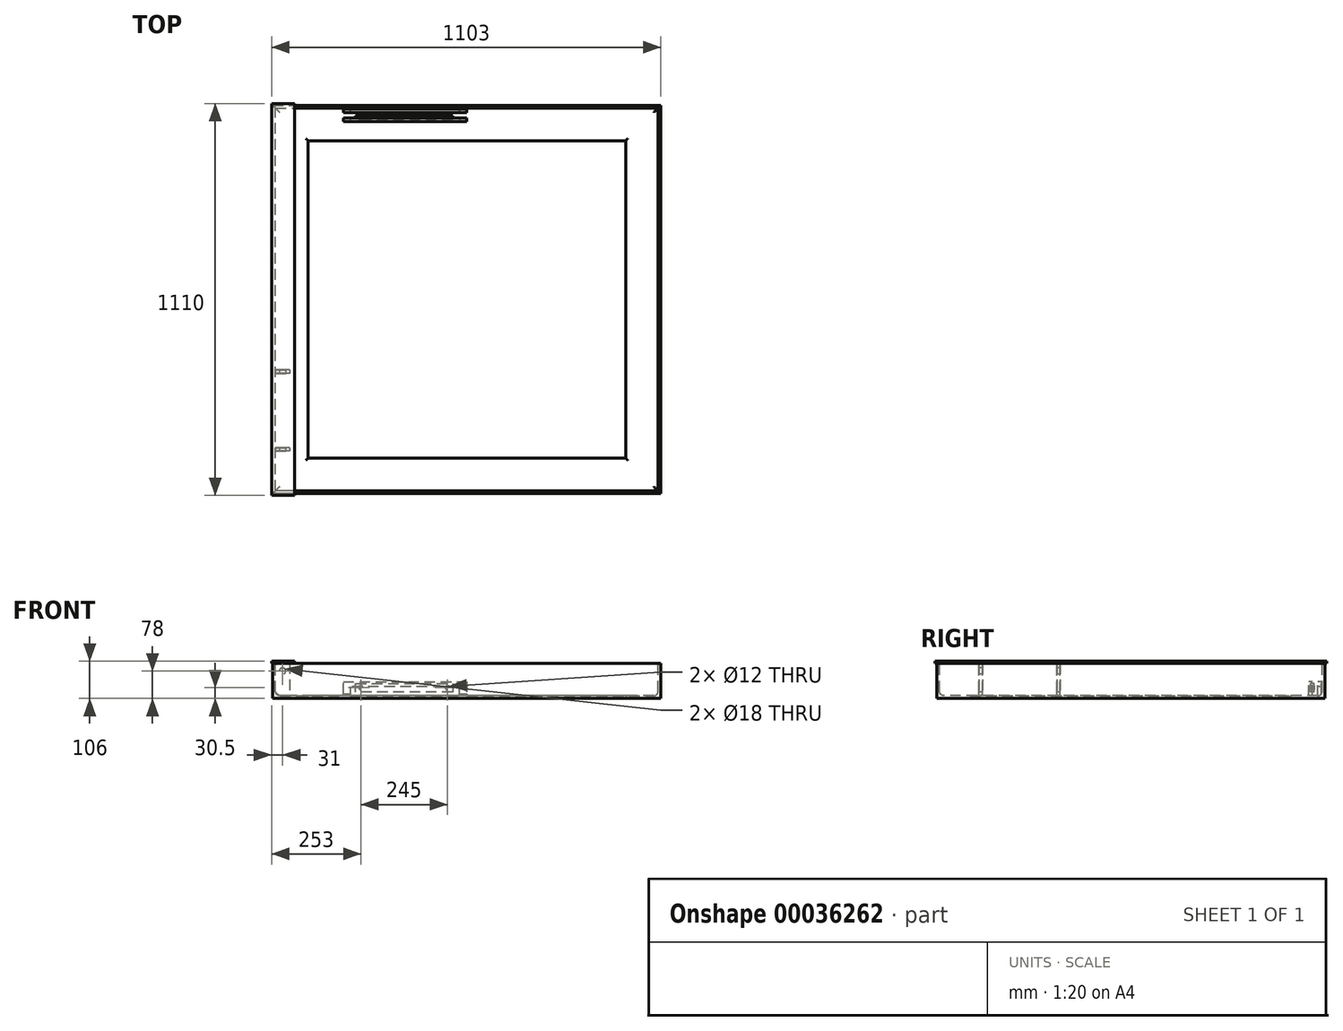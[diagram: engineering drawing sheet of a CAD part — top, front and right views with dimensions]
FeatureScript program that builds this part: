
annotation { "Feature Type Name" : "Feature", "Feature Type Description" : "" }
export const myFeature = defineFeature(function(context is Context, id is Id, definition is map)
    precondition{}
    {
        {
            var Q0;
            Q0=qCreatedBy(makeId("Top.planeOp"),FACE);
            var sketch = newSketch(context, id + "F0", { "sketchPlane" : qUnion([Q0])});
            skLineSegment(sketch, "E0.bottom", {"start": v(0, 0) * mm, "end": v(1100, 0) * mm});
            skLineSegment(sketch, "E0.top", {"start": v(0, 1100) * mm, "end": v(1100, 1100) * mm});
            skLineSegment(sketch, "E0.left", {"start": v(0, 0) * mm, "end": v(0, 1100) * mm});
            skLineSegment(sketch, "E0.right", {"start": v(1100, 0) * mm, "end": v(1100, 1100) * mm});
            skSolve(sketch);
        }
        {
            var Q0;
            Q0=qCreatedBy(makeId("Front.planeOp"),FACE);
            var sketch = newSketch(context, id + "F1", { "sketchPlane" : qUnion([Q0])});
            skLineSegment(sketch, "E1", {"start": v(0, 0) * mm, "end": v(0, -100) * mm});
            skLineSegment(sketch, "E2", {"start": v(0, -100) * mm, "end": v(100, -100) * mm});
            skLineSegment(sketch, "E3", {"start": v(100, -100) * mm, "end": v(100, -98) * mm});
            skLineSegment(sketch, "E4", {"start": v(94, -92) * mm, "end": v(20, -92) * mm});
            skLineSegment(sketch, "E5", {"start": v(8, -80) * mm, "end": v(8, -6) * mm});
            skLineSegment(sketch, "E6", {"start": v(2, 0) * mm, "end": v(0, 0) * mm});
            skPoint(sketch, "E7.visualSharp", {"position": v(8, -92) * mm});
            skArc(sketch, "E7.filletArc", {"start": v(8, -80) * mm, "mid": v(11.51, -88.49) * mm, "end": v(20, -92) * mm});
            skPoint(sketch, "E8.visualSharp", {"position": v(100, -92) * mm});
            skArc(sketch, "E8.filletArc", {"start": v(100, -98) * mm, "mid": v(98.24, -93.76) * mm, "end": v(94, -92) * mm});
            skPoint(sketch, "E9.visualSharp", {"position": v(8, 0) * mm});
            skArc(sketch, "E9.filletArc", {"start": v(8, -6) * mm, "mid": v(6.24, -1.76) * mm, "end": v(2, 0) * mm});
            skSolve(sketch);
        }
        {
            var Q0;
            Q0=makeQuery(id+"F1.imprint","IMPRINT",FACE,{"disambiguationData":[TD([[makeQuery(id+"F1.imprint","IMPRINT",EDGE,{"derivedFrom":sQuery(id+"F1.wireOp",EDGE,"E1")}),1.0]])]});
            var Q1;
            Q1=sQuery(id+"F0.wireOp",EDGE,"E0.left");
            var Q2;
            Q2=sQuery(id+"F0.wireOp",EDGE,"E0.top");
            var Q3;
            Q3=sQuery(id+"F0.wireOp",EDGE,"E0.right");
            var Q4;
            Q4=sQuery(id+"F0.wireOp",EDGE,"E0.bottom");
            sweep(context, id + "F2", {"profiles" : qUnion([Q0]), "path" : qUnion([Q1, Q2, Q3, Q4])});
        }
        {
            var Q0;
            Q0=makeQuery(id+"F0.imprint","IMPRINT",FACE,{"disambiguationData":[TD([[makeQuery(id+"F0.imprint","IMPRINT",EDGE,{"derivedFrom":sQuery(id+"F0.wireOp",EDGE,"E0.bottom")}),1.0]])]});
            var sketch = newSketch(context, id + "F3", { "sketchPlane" : qUnion([Q0])});
            skLineSegment(sketch, "E10", {"start": v(21.54, 120) * mm, "end": v(171.03, 120) * mm, "construction": true});
            skLineSegment(sketch, "E11", {"start": v(50, 167) * mm, "end": v(50, -35.97) * mm, "construction": true});
            skSolve(sketch);
        }
        {
            var Q0;
            Q0=sQuery(id+"F3.wireOp",EDGE,"E10");
            cPlane(context, id + "F4", {"entities" : qUnion([Q0]), "cplaneType" : CPlaneType.LINE_ANGLE, "offset" : 150 * mm, "angle" : 0 * degree, "width" : 150 * mm, "height" : 150 * mm});
        }
        {
            var Q0;
            Q0=qCreatedBy(id+"F4.planeOp",FACE);
            var sketch = newSketch(context, id + "F5", { "sketchPlane" : qUnion([Q0])});
            skLineSegment(sketch, "E12.MirrorCS", {"start": v(-48, -92) * mm, "end": v(-18.94, -92) * mm});
            skLineSegment(sketch, "E13.MirrorCS", {"start": v(-8, 0) * mm, "end": v(-48, 0) * mm});
            skCircle(sketch, "E14.MirrorC", {"center": v(-28, -22) * mm, "radius": 9 * mm});
            skLineSegment(sketch, "E15.MirrorCS", {"start": v(-8, -81.06) * mm, "end": v(-8, 0) * mm});
            skLineSegment(sketch, "E16.MirrorCS", {"start": v(-18.94, -92) * mm, "end": v(-8, -81.06) * mm});
            skLineSegment(sketch, "E17.MirrorCS", {"start": v(-48, 0) * mm, "end": v(-48, -92) * mm});
            skSolve(sketch);
        }
        {
            var Q0;
            Q0 = qSketchRegion(id + "F5", true);
            extrude(context, id + "F6", {"entities" : qUnion([Q0]), "depth" : 10 * mm});
        }
        {
            var Q0;
            Q0=makeQuery(id+"F6.opExtrude","SWEPT_BODY",BODY,{"disambiguationData":[OSD([sQuery(id+"F5.wireOp",EDGE,"E12.MirrorCS"),sQuery(id+"F5.wireOp",EDGE,"E13.MirrorCS"),sQuery(id+"F5.wireOp",EDGE,"E14.MirrorC"),sQuery(id+"F5.wireOp",EDGE,"E15.MirrorCS"),sQuery(id+"F5.wireOp",EDGE,"E16.MirrorCS"),sQuery(id+"F5.wireOp",EDGE,"E17.MirrorCS")])]});
            transform(context, id + "F7", {"entities" : qUnion([Q0]), "transformType" : TransformType.TRANSLATION_3D, "dx" : 0 * mm, "dy" : 220 * mm, "dz" : 0 * mm, "makeCopy" : true});
        }
        {
            var Q0;
            Q0=makeQuery(id+"F7.opPattern","COPY",EDGE,{"derivedFrom":makeQuery(id+"F6.opExtrude","CAP_EDGE",EDGE,{"disambiguationData":[OSD([sQuery(id+"F5.wireOp",EDGE,"E13.MirrorCS")])],"isStart":false}),"instanceName":"1"});
            cPlane(context, id + "F8", {"entities" : qUnion([Q0]), "cplaneType" : CPlaneType.LINE_ANGLE, "offset" : 150 * mm, "angle" : 0 * degree, "width" : 150 * mm, "height" : 150 * mm});
        }
        {
            var Q0;
            Q0=makeQuery(id+"F3.imprint","IMPRINT",FACE,{"disambiguationData":[TD([[makeQuery(id+"F3.imprint","IMPRINT",EDGE,{"derivedFrom":makeQuery(id+"F0.imprint","IMPRINT",EDGE,{"derivedFrom":sQuery(id+"F0.wireOp",EDGE,"E0.bottom")})}),1.0]])]});
            var sketch = newSketch(context, id + "F9", { "sketchPlane" : qUnion([Q0])});
            skLineSegment(sketch, "E18.bottom", {"start": v(-3, 1105) * mm, "end": v(62, 1105) * mm});
            skLineSegment(sketch, "E18.top", {"start": v(-3, -5) * mm, "end": v(62, -5) * mm});
            skLineSegment(sketch, "E18.left", {"start": v(-3, 1105) * mm, "end": v(-3, -5) * mm});
            skLineSegment(sketch, "E18.right", {"start": v(62, 1105) * mm, "end": v(62, -5) * mm});
            skSolve(sketch);
        }
        {
            var Q0;
            Q0 = qSketchRegion(id + "F9", true);
            extrude(context, id + "F10", {"entities" : qUnion([Q0]), "depth" : 6 * mm});
        }
        {
            var Q0;
            Q0=qCreatedBy(id+"F8.planeOp",FACE);
            cPlane(context, id + "F11", {"entities" : qUnion([Q0]), "cplaneType" : CPlaneType.OFFSET, "offset" : 710 * mm, "width" : 150 * mm, "height" : 150 * mm});
        }
        {
            var Q0;
            Q0=qCreatedBy(id+"F11.planeOp",FACE);
            var sketch = newSketch(context, id + "F12", { "sketchPlane" : qUnion([Q0])});
            skLineSegment(sketch, "E19", {"start": v(-235, -82) * mm, "end": v(-235, -57) * mm});
            skLineSegment(sketch, "E20", {"start": v(-235, -57) * mm, "end": v(-510, -57) * mm});
            skLineSegment(sketch, "E21", {"start": v(-510, -57) * mm, "end": v(-510, -82) * mm});
            skLineSegment(sketch, "E22", {"start": v(-510, -82) * mm, "end": v(-235, -82) * mm});
            skCircle(sketch, "E23", {"center": v(-250, -69.5) * mm, "radius": 6 * mm});
            skLineSegment(sketch, "E24", {"start": v(-372.5, -31.33) * mm, "end": v(-372.5, -111.75) * mm, "construction": true});
            skCircle(sketch, "E25.MirrorC", {"center": v(-495, -69.5) * mm, "radius": 6 * mm});
            skSolve(sketch);
        }
        {
            var Q0;
            Q0 = qSketchRegion(id + "F12", true);
            extrude(context, id + "F13", {"entities" : qUnion([Q0]), "depth" : 10 * mm});
        }
        {
            var Q0;
            Q0=qCreatedBy(id+"F11.planeOp",FACE);
            cPlane(context, id + "F14", {"entities" : qUnion([Q0]), "cplaneType" : CPlaneType.OFFSET, "offset" : 20 * mm, "width" : 150 * mm, "height" : 150 * mm});
        }
        {
            var Q0;
            Q0=qCreatedBy(id+"F14.planeOp",FACE);
            var sketch = newSketch(context, id + "F15", { "sketchPlane" : qUnion([Q0])});
            skLineSegment(sketch, "E26", {"start": v(-200, -92) * mm, "end": v(-200, -52) * mm});
            skLineSegment(sketch, "E27", {"start": v(-200, -52) * mm, "end": v(-550, -52) * mm});
            skLineSegment(sketch, "E28", {"start": v(-550, -52) * mm, "end": v(-550, -92) * mm});
            skLineSegment(sketch, "E29", {"start": v(-550, -92) * mm, "end": v(-530, -92) * mm});
            skLineSegment(sketch, "E30", {"start": v(-530, -92) * mm, "end": v(-530, -67) * mm});
            skLineSegment(sketch, "E31", {"start": v(-530, -67) * mm, "end": v(-220, -67) * mm});
            skLineSegment(sketch, "E32", {"start": v(-220, -67) * mm, "end": v(-220, -92) * mm});
            skLineSegment(sketch, "E33", {"start": v(-220, -92) * mm, "end": v(-200, -92) * mm});
            skSolve(sketch);
        }
        {
            var Q0;
            Q0 = qSketchRegion(id + "F15", true);
            extrude(context, id + "F16", {"entities" : qUnion([Q0]), "operationType" : NewBodyOperationType.ADD, "depth" : 10 * mm});
        }
        {
            var Q0;
            Q0=qCreatedBy(id+"F14.planeOp",FACE);
            cPlane(context, id + "F17", {"entities" : qUnion([Q0]), "cplaneType" : CPlaneType.OFFSET, "offset" : 25.62 * mm, "oppositeDirection" : true, "width" : 150 * mm, "height" : 150 * mm});
        }
        {
            var Q0;
            Q0=qCreatedBy(id+"F17.planeOp",FACE);
            var sketch = newSketch(context, id + "F18", { "sketchPlane" : qUnion([Q0])});
            skLineSegment(sketch, "E34", {"start": v(-200, -92) * mm, "end": v(-200, -52) * mm});
            skLineSegment(sketch, "E35", {"start": v(-200, -52) * mm, "end": v(-550, -52) * mm});
            skLineSegment(sketch, "E36", {"start": v(-550, -52) * mm, "end": v(-550, -92) * mm});
            skLineSegment(sketch, "E37", {"start": v(-550, -92) * mm, "end": v(-530, -92) * mm});
            skLineSegment(sketch, "E38", {"start": v(-530, -92) * mm, "end": v(-530, -67) * mm});
            skLineSegment(sketch, "E39", {"start": v(-530, -67) * mm, "end": v(-220, -67) * mm});
            skLineSegment(sketch, "E40", {"start": v(-220, -67) * mm, "end": v(-220, -92) * mm});
            skLineSegment(sketch, "E41", {"start": v(-220, -92) * mm, "end": v(-200, -92) * mm});
            skSolve(sketch);
        }
        {
            var Q0;
            Q0 = qSketchRegion(id + "F18", true);
            extrude(context, id + "F19", {"entities" : qUnion([Q0]), "depth" : 10 * mm});
        }
    });
